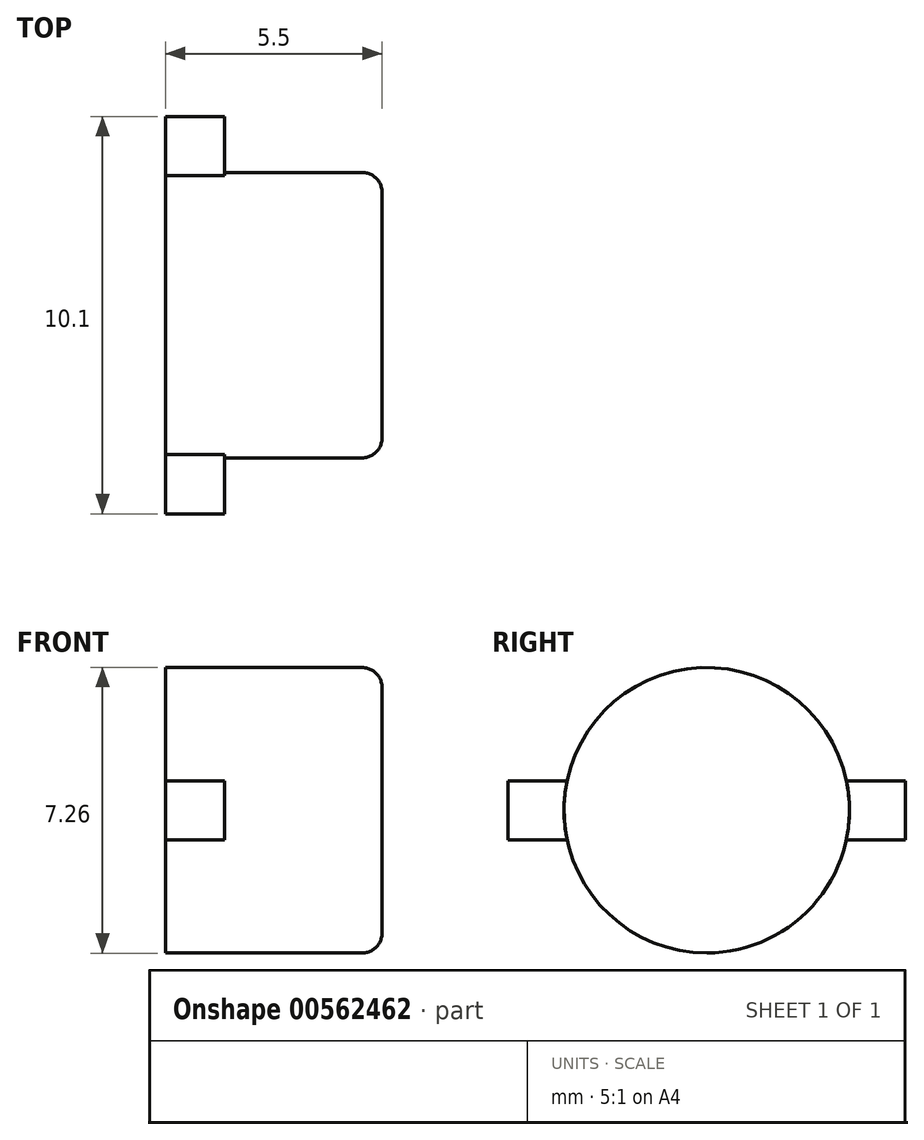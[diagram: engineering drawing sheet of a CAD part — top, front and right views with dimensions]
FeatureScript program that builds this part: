
annotation { "Feature Type Name" : "Feature", "Feature Type Description" : "" }
export const myFeature = defineFeature(function(context is Context, id is Id, definition is map)
    precondition{}
    {
        {
            var Q0;
            Q0=qCreatedBy(makeId("Right.planeOp"),FACE);
            var sketch = newSketch(context, id + "F0", { "sketchPlane" : qUnion([Q0])});
            skCircle(sketch, "E0", {"center": v(0, 0) * mm, "radius": 3.62 * mm});
            skSolve(sketch);
        }
        {
            var Q0;
            Q0=makeQuery(id+"F0.imprint","IMPRINT",FACE,{"disambiguationData":[TD([[makeQuery(id+"F0.imprint","IMPRINT",EDGE,{"derivedFrom":sQuery(id+"F0.wireOp",EDGE,"E0")}),1.0]])]});
            extrude(context, id + "F1", {"entities" : qUnion([Q0]), "depth" : 5.5 * mm, "offsetDistance" : 25 * mm, "symmetric" : true});
        }
        {
            var Q0;
            Q0=makeQuery(id+"F1.opExtrude","CAP_FACE",FACE,{"disambiguationData":[OSD([sQuery(id+"F0.wireOp",EDGE,"E0")])],"isStart":false});
            fillet(context, id + "F2", {"entities" : qUnion([Q0]), "radius" : 0.5 * mm, "tangentPropagation" : true, "allowEdgeOverflow" : false});
        }
        {
            var Q0;
            Q0=makeQuery(id+"F1.opExtrude","CAP_FACE",FACE,{"disambiguationData":[OSD([sQuery(id+"F0.wireOp",EDGE,"E0")])],"isStart":true});
            var sketch = newSketch(context, id + "F3", { "sketchPlane" : qUnion([Q0])});
            skLineSegment(sketch, "E1.left", {"start": v(5.05, -0.75) * mm, "end": v(5.05, 0.75) * mm});
            skLineSegment(sketch, "E2.left", {"start": v(-5.05, 0.75) * mm, "end": v(-5.05, -0.75) * mm});
            skLineSegment(sketch, "E3", {"start": v(5.05, 0.75) * mm, "end": v(3.55, 0.75) * mm});
            skLineSegment(sketch, "E4", {"start": v(5.05, -0.75) * mm, "end": v(3.55, -0.75) * mm});
            skArc(sketch, "E5", {"start": v(-3.55, 0.75) * mm, "mid": v(-3.63, 0) * mm, "end": v(-3.55, -0.75) * mm});
            skLineSegment(sketch, "E6", {"start": v(-5.05, 0.75) * mm, "end": v(-3.55, 0.75) * mm});
            skLineSegment(sketch, "E7", {"start": v(-5.05, -0.75) * mm, "end": v(-3.55, -0.75) * mm});
            skArc(sketch, "E8.trimOffspring", {"start": v(3.55, -0.75) * mm, "mid": v(3.63, 0) * mm, "end": v(3.55, 0.75) * mm});
            skPoint(sketch, "E9", {"position": v(5.05, 0) * mm});
            skPoint(sketch, "E10", {"position": v(-5.05, 0) * mm});
            skSolve(sketch);
        }
        {
            var Q0;
            Q0=qSketchRegion(id+"F3",true);
            extrude(context, id + "F4", {"entities" : qUnion([Q0]), "operationType" : NewBodyOperationType.ADD, "oppositeDirection" : true, "depth" : 1.5 * mm, "offsetDistance" : 25 * mm});
        }
    });
